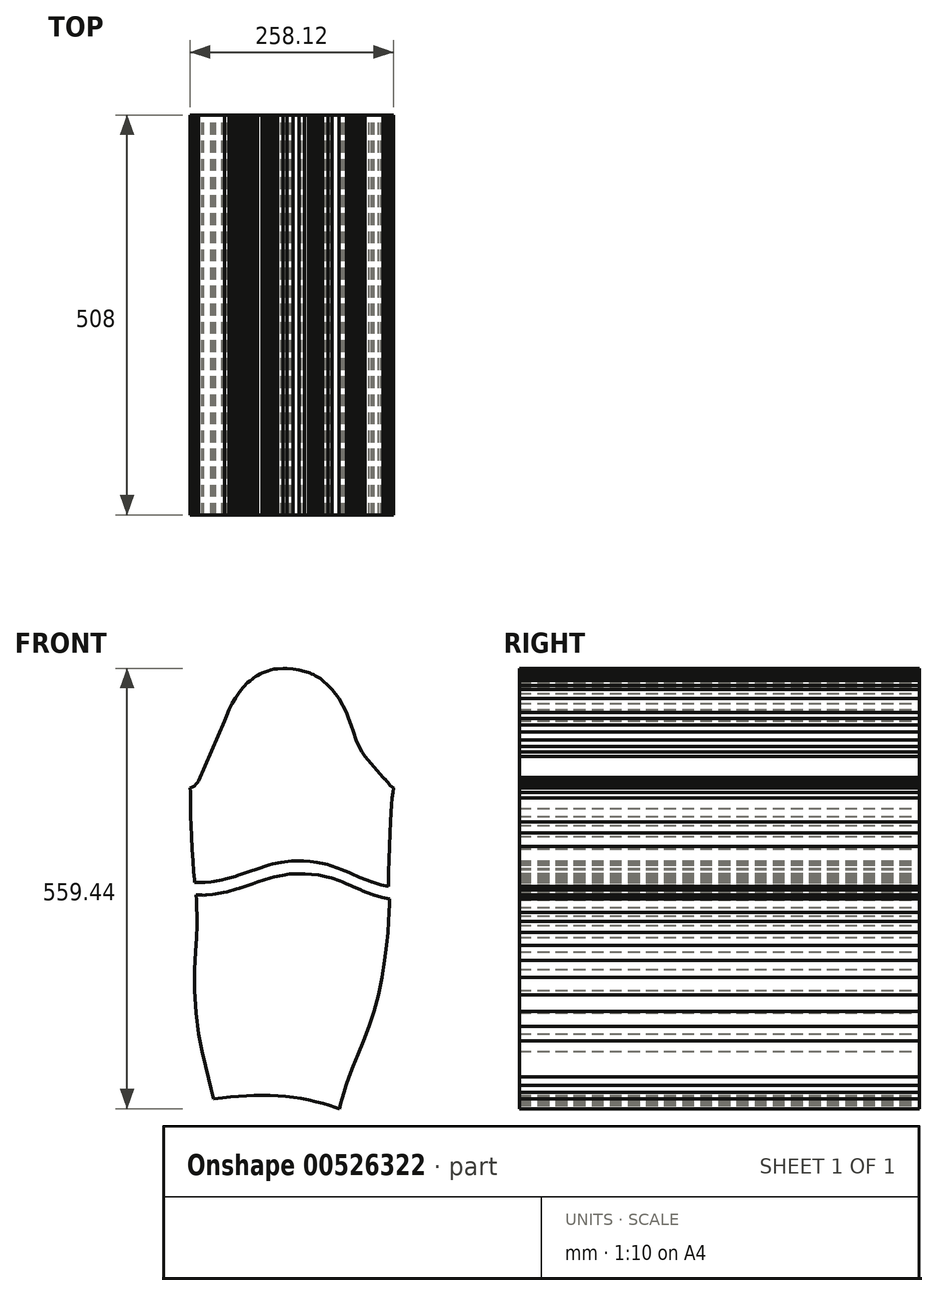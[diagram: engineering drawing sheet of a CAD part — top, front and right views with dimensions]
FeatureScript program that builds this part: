
annotation { "Feature Type Name" : "Feature", "Feature Type Description" : "" }
export const myFeature = defineFeature(function(context is Context, id is Id, definition is map)
    precondition{}
    {
        {
            var Q0;
            Q0=qCreatedBy(makeId("Front.planeOp"),FACE);
            var sketch = newSketch(context, id + "F0", { "sketchPlane" : qUnion([Q0])});
            skLineSegment(sketch, "E0", {"start": v(-129.06, 127.99) * mm, "end": v(-125.78, 128.92) * mm});
            skLineSegment(sketch, "E1", {"start": v(-125.78, 128.92) * mm, "end": v(-123.74, 130.52) * mm});
            skLineSegment(sketch, "E2", {"start": v(-123.74, 130.52) * mm, "end": v(-121.67, 132.71) * mm});
            skLineSegment(sketch, "E3", {"start": v(-121.67, 132.71) * mm, "end": v(-119.92, 134.96) * mm});
            skLineSegment(sketch, "E4", {"start": v(-119.92, 134.96) * mm, "end": v(-118.45, 136.86) * mm});
            skLineSegment(sketch, "E5", {"start": v(-118.45, 136.86) * mm, "end": v(-85.06, 212.65) * mm});
            skLineSegment(sketch, "E6", {"start": v(-85.06, 212.65) * mm, "end": v(-82.6, 219.33) * mm});
            skLineSegment(sketch, "E7", {"start": v(-82.6, 219.33) * mm, "end": v(-79.7, 227.1) * mm});
            skLineSegment(sketch, "E8", {"start": v(-79.7, 227.1) * mm, "end": v(-75.87, 235.03) * mm});
            skLineSegment(sketch, "E9", {"start": v(-75.87, 235.03) * mm, "end": v(-71.47, 242.22) * mm});
            skLineSegment(sketch, "E10", {"start": v(-71.47, 242.22) * mm, "end": v(-67.32, 247.98) * mm});
            skLineSegment(sketch, "E11", {"start": v(-67.32, 247.98) * mm, "end": v(-64.18, 252.12) * mm});
            skLineSegment(sketch, "E12", {"start": v(-64.18, 252.12) * mm, "end": v(-61.7, 255.53) * mm});
            skLineSegment(sketch, "E13", {"start": v(-61.7, 255.53) * mm, "end": v(-59.4, 257.84) * mm});
            skLineSegment(sketch, "E14", {"start": v(-59.4, 257.84) * mm, "end": v(-58.19, 259.5) * mm});
            skLineSegment(sketch, "E15", {"start": v(-58.19, 259.5) * mm, "end": v(-56.4, 261.46) * mm});
            skLineSegment(sketch, "E16", {"start": v(-56.4, 261.46) * mm, "end": v(-53.2, 263.83) * mm});
            skLineSegment(sketch, "E17", {"start": v(-53.2, 263.83) * mm, "end": v(-50.06, 266.24) * mm});
            skLineSegment(sketch, "E18", {"start": v(-50.06, 266.24) * mm, "end": v(-48.03, 267.92) * mm});
            skLineSegment(sketch, "E19", {"start": v(-48.03, 267.92) * mm, "end": v(-45.8, 269.31) * mm});
            skLineSegment(sketch, "E20", {"start": v(-45.8, 269.31) * mm, "end": v(-43.72, 270.77) * mm});
            skLineSegment(sketch, "E21", {"start": v(-43.72, 270.77) * mm, "end": v(-40.37, 272.52) * mm});
            skLineSegment(sketch, "E22", {"start": v(-40.37, 272.52) * mm, "end": v(-37.71, 273.92) * mm});
            skLineSegment(sketch, "E23", {"start": v(-37.71, 273.92) * mm, "end": v(-33.9, 275.3) * mm});
            skLineSegment(sketch, "E24", {"start": v(-33.9, 275.3) * mm, "end": v(-30.01, 276.47) * mm});
            skLineSegment(sketch, "E25", {"start": v(-30.01, 276.47) * mm, "end": v(-27.04, 277.54) * mm});
            skLineSegment(sketch, "E26", {"start": v(-27.04, 277.54) * mm, "end": v(-22.6, 278.6) * mm});
            skLineSegment(sketch, "E27", {"start": v(-22.6, 278.6) * mm, "end": v(-17.94, 279.04) * mm});
            skLineSegment(sketch, "E28", {"start": v(-17.94, 279.04) * mm, "end": v(-11.4, 279.5) * mm});
            skLineSegment(sketch, "E29", {"start": v(-11.4, 279.5) * mm, "end": v(-5.8, 279.72) * mm});
            skLineSegment(sketch, "E30", {"start": v(-5.8, 279.72) * mm, "end": v(1.6, 279.03) * mm});
            skLineSegment(sketch, "E31", {"start": v(1.6, 279.03) * mm, "end": v(9.41, 277.6) * mm});
            skLineSegment(sketch, "E32", {"start": v(9.41, 277.6) * mm, "end": v(16.28, 275.7) * mm});
            skLineSegment(sketch, "E33", {"start": v(16.28, 275.7) * mm, "end": v(21.23, 274.15) * mm});
            skLineSegment(sketch, "E34", {"start": v(21.23, 274.15) * mm, "end": v(23.5, 273.55) * mm});
            skLineSegment(sketch, "E35", {"start": v(23.5, 273.55) * mm, "end": v(25.19, 272.62) * mm});
            skLineSegment(sketch, "E36", {"start": v(25.19, 272.62) * mm, "end": v(27.5, 271.6) * mm});
            skLineSegment(sketch, "E37", {"start": v(27.5, 271.6) * mm, "end": v(30.25, 269.98) * mm});
            skLineSegment(sketch, "E38", {"start": v(30.25, 269.98) * mm, "end": v(32.91, 268.54) * mm});
            skLineSegment(sketch, "E39", {"start": v(32.91, 268.54) * mm, "end": v(36.27, 266.46) * mm});
            skLineSegment(sketch, "E40", {"start": v(36.27, 266.46) * mm, "end": v(39.3, 263.93) * mm});
            skLineSegment(sketch, "E41", {"start": v(39.3, 263.93) * mm, "end": v(46.3, 257.73) * mm});
            skLineSegment(sketch, "E42", {"start": v(46.3, 257.73) * mm, "end": v(51.38, 252.95) * mm});
            skLineSegment(sketch, "E43", {"start": v(51.38, 252.95) * mm, "end": v(55.72, 247.02) * mm});
            skLineSegment(sketch, "E44", {"start": v(55.72, 247.02) * mm, "end": v(59.84, 241.45) * mm});
            skLineSegment(sketch, "E45", {"start": v(59.84, 241.45) * mm, "end": v(69.25, 223.53) * mm});
            skLineSegment(sketch, "E46", {"start": v(69.25, 223.53) * mm, "end": v(71.89, 216.2) * mm});
            skLineSegment(sketch, "E47", {"start": v(71.89, 216.2) * mm, "end": v(75.36, 208) * mm});
            skLineSegment(sketch, "E48", {"start": v(75.36, 208) * mm, "end": v(78.39, 198.63) * mm});
            skLineSegment(sketch, "E49", {"start": v(78.39, 198.63) * mm, "end": v(81.28, 188.97) * mm});
            skLineSegment(sketch, "E50", {"start": v(81.28, 188.97) * mm, "end": v(85.37, 180.55) * mm});
            skLineSegment(sketch, "E51", {"start": v(85.37, 180.55) * mm, "end": v(89.27, 173.34) * mm});
            skLineSegment(sketch, "E52", {"start": v(89.27, 173.34) * mm, "end": v(93, 167.63) * mm});
            skLineSegment(sketch, "E53", {"start": v(93, 167.63) * mm, "end": v(116.08, 141.22) * mm});
            skLineSegment(sketch, "E54", {"start": v(116.08, 141.22) * mm, "end": v(117.67, 139.44) * mm});
            skLineSegment(sketch, "E55", {"start": v(117.67, 139.44) * mm, "end": v(118.96, 138.2) * mm});
            skLineSegment(sketch, "E56", {"start": v(118.96, 138.2) * mm, "end": v(120.13, 136.65) * mm});
            skLineSegment(sketch, "E57", {"start": v(120.13, 136.65) * mm, "end": v(121.99, 134.64) * mm});
            skLineSegment(sketch, "E58", {"start": v(121.99, 134.64) * mm, "end": v(124.73, 131.11) * mm});
            skLineSegment(sketch, "E59", {"start": v(124.73, 131.11) * mm, "end": v(129.06, 127.9) * mm});
            skLineSegment(sketch, "E60", {"start": v(129.06, 127.9) * mm, "end": v(128.28, 121.94) * mm});
            skLineSegment(sketch, "E61", {"start": v(128.28, 121.94) * mm, "end": v(127.6, 114.85) * mm});
            skLineSegment(sketch, "E62", {"start": v(127.6, 114.85) * mm, "end": v(126.92, 106.4) * mm});
            skLineSegment(sketch, "E63", {"start": v(126.92, 106.4) * mm, "end": v(126.18, 96.34) * mm});
            skLineSegment(sketch, "E64", {"start": v(126.18, 96.34) * mm, "end": v(125.4, 84.41) * mm});
            skLineSegment(sketch, "E65", {"start": v(125.4, 84.41) * mm, "end": v(124.62, 70.26) * mm});
            skLineSegment(sketch, "E66", {"start": v(124.62, 70.26) * mm, "end": v(123.94, 53.44) * mm});
            skLineSegment(sketch, "E67", {"start": v(123.94, 53.44) * mm, "end": v(123.45, 36.05) * mm});
            skLineSegment(sketch, "E68", {"start": v(123.45, 36.05) * mm, "end": v(123.1, 20.74) * mm});
            skLineSegment(sketch, "E69", {"start": v(123.1, 20.74) * mm, "end": v(122.77, 7.64) * mm});
            skLineSegment(sketch, "E70", {"start": v(122.77, 7.64) * mm, "end": v(122.6, 2.87) * mm});
            skLineSegment(sketch, "E71", {"start": v(122.6, 2.87) * mm, "end": v(116.26, 4.18) * mm});
            skLineSegment(sketch, "E72", {"start": v(116.26, 4.18) * mm, "end": v(113.1, 4.8) * mm});
            skLineSegment(sketch, "E73", {"start": v(113.1, 4.8) * mm, "end": v(102, 8.01) * mm});
            skLineSegment(sketch, "E74", {"start": v(102, 8.01) * mm, "end": v(101.15, 8.25) * mm});
            skLineSegment(sketch, "E75", {"start": v(101.15, 8.25) * mm, "end": v(100.98, 8.32) * mm});
            skLineSegment(sketch, "E76", {"start": v(100.98, 8.32) * mm, "end": v(100.06, 8.68) * mm});
            skLineSegment(sketch, "E77", {"start": v(100.06, 8.68) * mm, "end": v(88.25, 13.28) * mm});
            skLineSegment(sketch, "E78", {"start": v(88.25, 13.28) * mm, "end": v(86.15, 14.09) * mm});
            skLineSegment(sketch, "E79", {"start": v(86.15, 14.09) * mm, "end": v(75.3, 18.88) * mm});
            skLineSegment(sketch, "E80", {"start": v(75.3, 18.88) * mm, "end": v(72.52, 20.08) * mm});
            skLineSegment(sketch, "E81", {"start": v(72.52, 20.08) * mm, "end": v(67.7, 22.18) * mm});
            skLineSegment(sketch, "E82", {"start": v(67.7, 22.18) * mm, "end": v(62.7, 24.37) * mm});
            skLineSegment(sketch, "E83", {"start": v(62.7, 24.37) * mm, "end": v(59.36, 25.76) * mm});
            skLineSegment(sketch, "E84", {"start": v(59.36, 25.76) * mm, "end": v(48.53, 29.38) * mm});
            skLineSegment(sketch, "E85", {"start": v(48.53, 29.38) * mm, "end": v(45.64, 30.34) * mm});
            skLineSegment(sketch, "E86", {"start": v(45.64, 30.34) * mm, "end": v(42.36, 31.17) * mm});
            skLineSegment(sketch, "E87", {"start": v(42.36, 31.17) * mm, "end": v(32.12, 33.1) * mm});
            skLineSegment(sketch, "E88", {"start": v(32.12, 33.1) * mm, "end": v(23.04, 34.23) * mm});
            skLineSegment(sketch, "E89", {"start": v(23.04, 34.23) * mm, "end": v(15.13, 34.8) * mm});
            skLineSegment(sketch, "E90", {"start": v(15.13, 34.8) * mm, "end": v(-0.5, 34.69) * mm});
            skLineSegment(sketch, "E91", {"start": v(-0.5, 34.69) * mm, "end": v(-4.82, 34.6) * mm});
            skLineSegment(sketch, "E92", {"start": v(-4.82, 34.6) * mm, "end": v(-13.8, 32.87) * mm});
            skLineSegment(sketch, "E93", {"start": v(-13.8, 32.87) * mm, "end": v(-24.33, 30.99) * mm});
            skLineSegment(sketch, "E94", {"start": v(-24.33, 30.99) * mm, "end": v(-28.64, 29.75) * mm});
            skLineSegment(sketch, "E95", {"start": v(-28.64, 29.75) * mm, "end": v(-45.2, 24.49) * mm});
            skLineSegment(sketch, "E96", {"start": v(-45.2, 24.49) * mm, "end": v(-51.53, 22.25) * mm});
            skLineSegment(sketch, "E97", {"start": v(-51.53, 22.25) * mm, "end": v(-66.86, 16.9) * mm});
            skLineSegment(sketch, "E98", {"start": v(-66.86, 16.9) * mm, "end": v(-67.43, 16.71) * mm});
            skLineSegment(sketch, "E99", {"start": v(-67.43, 16.71) * mm, "end": v(-68.62, 16.33) * mm});
            skLineSegment(sketch, "E100", {"start": v(-68.62, 16.33) * mm, "end": v(-71.7, 15.5) * mm});
            skLineSegment(sketch, "E101", {"start": v(-71.7, 15.5) * mm, "end": v(-84, 12.04) * mm});
            skLineSegment(sketch, "E102", {"start": v(-84, 12.04) * mm, "end": v(-88.47, 11.04) * mm});
            skLineSegment(sketch, "E103", {"start": v(-88.47, 11.04) * mm, "end": v(-98.66, 9.15) * mm});
            skLineSegment(sketch, "E104", {"start": v(-98.66, 9.15) * mm, "end": v(-102.44, 8.55) * mm});
            skLineSegment(sketch, "E105", {"start": v(-102.44, 8.55) * mm, "end": v(-110.4, 7.93) * mm});
            skLineSegment(sketch, "E106", {"start": v(-110.4, 7.93) * mm, "end": v(-113.6, 7.68) * mm});
            skLineSegment(sketch, "E107", {"start": v(-113.6, 7.68) * mm, "end": v(-116.64, 7.7) * mm});
            skLineSegment(sketch, "E108", {"start": v(-116.64, 7.7) * mm, "end": v(-123.46, 7.78) * mm});
            skLineSegment(sketch, "E109", {"start": v(-123.46, 7.78) * mm, "end": v(-123.66, 10.72) * mm});
            skLineSegment(sketch, "E110", {"start": v(-123.66, 10.72) * mm, "end": v(-124.49, 21.76) * mm});
            skLineSegment(sketch, "E111", {"start": v(-124.49, 21.76) * mm, "end": v(-125.5, 34.65) * mm});
            skLineSegment(sketch, "E112", {"start": v(-125.5, 34.65) * mm, "end": v(-126.62, 50.2) * mm});
            skLineSegment(sketch, "E113", {"start": v(-126.62, 50.2) * mm, "end": v(-127.52, 66.05) * mm});
            skLineSegment(sketch, "E114", {"start": v(-127.52, 66.05) * mm, "end": v(-128.1, 79.86) * mm});
            skLineSegment(sketch, "E115", {"start": v(-128.1, 79.86) * mm, "end": v(-128.43, 91.56) * mm});
            skLineSegment(sketch, "E116", {"start": v(-128.43, 91.56) * mm, "end": v(-128.6, 101.4) * mm});
            skLineSegment(sketch, "E117", {"start": v(-128.6, 101.4) * mm, "end": v(-128.65, 109.84) * mm});
            skLineSegment(sketch, "E118", {"start": v(-128.65, 109.84) * mm, "end": v(-128.7, 116.9) * mm});
            skLineSegment(sketch, "E119", {"start": v(-128.7, 116.9) * mm, "end": v(-128.76, 122.9) * mm});
            skLineSegment(sketch, "E120", {"start": v(-128.76, 122.9) * mm, "end": v(-129.06, 127.99) * mm});
            skLineSegment(sketch, "E121", {"start": v(-87.7, -265.91) * mm, "end": v(-99.36, -267.16) * mm});
            skLineSegment(sketch, "E122", {"start": v(-99.36, -267.16) * mm, "end": v(-102.24, -254.86) * mm});
            skLineSegment(sketch, "E123", {"start": v(-102.24, -254.86) * mm, "end": v(-105.54, -241.28) * mm});
            skLineSegment(sketch, "E124", {"start": v(-105.54, -241.28) * mm, "end": v(-109.4, -225.58) * mm});
            skLineSegment(sketch, "E125", {"start": v(-109.4, -225.58) * mm, "end": v(-113.8, -207) * mm});
            skLineSegment(sketch, "E126", {"start": v(-113.8, -207) * mm, "end": v(-118.22, -184.67) * mm});
            skLineSegment(sketch, "E127", {"start": v(-118.22, -184.67) * mm, "end": v(-121.8, -157.96) * mm});
            skLineSegment(sketch, "E128", {"start": v(-121.8, -157.96) * mm, "end": v(-123.6, -129.31) * mm});
            skLineSegment(sketch, "E129", {"start": v(-123.6, -129.31) * mm, "end": v(-123.45, -102.96) * mm});
            skLineSegment(sketch, "E130", {"start": v(-123.45, -102.96) * mm, "end": v(-122.29, -80.62) * mm});
            skLineSegment(sketch, "E131", {"start": v(-122.29, -80.62) * mm, "end": v(-121.14, -62.26) * mm});
            skLineSegment(sketch, "E132", {"start": v(-121.14, -62.26) * mm, "end": v(-120.48, -47.14) * mm});
            skLineSegment(sketch, "E133", {"start": v(-120.48, -47.14) * mm, "end": v(-120.42, -34.55) * mm});
            skLineSegment(sketch, "E134", {"start": v(-120.42, -34.55) * mm, "end": v(-120.76, -23.9) * mm});
            skLineSegment(sketch, "E135", {"start": v(-120.76, -23.9) * mm, "end": v(-121.24, -14.8) * mm});
            skLineSegment(sketch, "E136", {"start": v(-121.24, -14.8) * mm, "end": v(-121.67, -8.4) * mm});
            skLineSegment(sketch, "E137", {"start": v(-121.67, -8.4) * mm, "end": v(-114.85, -8.49) * mm});
            skLineSegment(sketch, "E138", {"start": v(-114.85, -8.49) * mm, "end": v(-111.81, -8.5) * mm});
            skLineSegment(sketch, "E139", {"start": v(-111.81, -8.5) * mm, "end": v(-108.62, -8.26) * mm});
            skLineSegment(sketch, "E140", {"start": v(-108.62, -8.26) * mm, "end": v(-100.65, -7.64) * mm});
            skLineSegment(sketch, "E141", {"start": v(-100.65, -7.64) * mm, "end": v(-96.86, -7.03) * mm});
            skLineSegment(sketch, "E142", {"start": v(-96.86, -7.03) * mm, "end": v(-86.68, -5.15) * mm});
            skLineSegment(sketch, "E143", {"start": v(-86.68, -5.15) * mm, "end": v(-82.2, -4.15) * mm});
            skLineSegment(sketch, "E144", {"start": v(-82.2, -4.15) * mm, "end": v(-69.9, -0.7) * mm});
            skLineSegment(sketch, "E145", {"start": v(-69.9, -0.7) * mm, "end": v(-66.82, 0.15) * mm});
            skLineSegment(sketch, "E146", {"start": v(-66.82, 0.15) * mm, "end": v(-65.63, 0.53) * mm});
            skLineSegment(sketch, "E147", {"start": v(-65.63, 0.53) * mm, "end": v(-65.07, 0.72) * mm});
            skLineSegment(sketch, "E148", {"start": v(-65.07, 0.72) * mm, "end": v(-49.74, 6.07) * mm});
            skLineSegment(sketch, "E149", {"start": v(-49.74, 6.07) * mm, "end": v(-43.4, 8.3) * mm});
            skLineSegment(sketch, "E150", {"start": v(-43.4, 8.3) * mm, "end": v(-26.85, 13.57) * mm});
            skLineSegment(sketch, "E151", {"start": v(-26.85, 13.57) * mm, "end": v(-22.54, 14.8) * mm});
            skLineSegment(sketch, "E152", {"start": v(-22.54, 14.8) * mm, "end": v(-12, 16.69) * mm});
            skLineSegment(sketch, "E153", {"start": v(-12, 16.69) * mm, "end": v(-3.03, 18.4) * mm});
            skLineSegment(sketch, "E154", {"start": v(-3.03, 18.4) * mm, "end": v(1.3, 18.5) * mm});
            skLineSegment(sketch, "E155", {"start": v(1.3, 18.5) * mm, "end": v(16.93, 18.62) * mm});
            skLineSegment(sketch, "E156", {"start": v(16.93, 18.62) * mm, "end": v(24.83, 18.05) * mm});
            skLineSegment(sketch, "E157", {"start": v(24.83, 18.05) * mm, "end": v(33.92, 16.92) * mm});
            skLineSegment(sketch, "E158", {"start": v(33.92, 16.92) * mm, "end": v(44.15, 14.98) * mm});
            skLineSegment(sketch, "E159", {"start": v(44.15, 14.98) * mm, "end": v(47.44, 14.16) * mm});
            skLineSegment(sketch, "E160", {"start": v(47.44, 14.16) * mm, "end": v(50.33, 13.2) * mm});
            skLineSegment(sketch, "E161", {"start": v(50.33, 13.2) * mm, "end": v(61.15, 9.58) * mm});
            skLineSegment(sketch, "E162", {"start": v(61.15, 9.58) * mm, "end": v(64.49, 8.19) * mm});
            skLineSegment(sketch, "E163", {"start": v(64.49, 8.19) * mm, "end": v(69.5, 6) * mm});
            skLineSegment(sketch, "E164", {"start": v(69.5, 6) * mm, "end": v(74.32, 3.9) * mm});
            skLineSegment(sketch, "E165", {"start": v(74.32, 3.9) * mm, "end": v(77.09, 2.7) * mm});
            skLineSegment(sketch, "E166", {"start": v(77.09, 2.7) * mm, "end": v(87.94, -2.1) * mm});
            skLineSegment(sketch, "E167", {"start": v(87.94, -2.1) * mm, "end": v(90.05, -2.9) * mm});
            skLineSegment(sketch, "E168", {"start": v(90.05, -2.9) * mm, "end": v(101.85, -7.5) * mm});
            skLineSegment(sketch, "E169", {"start": v(101.85, -7.5) * mm, "end": v(102.77, -7.87) * mm});
            skLineSegment(sketch, "E170", {"start": v(102.77, -7.87) * mm, "end": v(102.94, -7.93) * mm});
            skLineSegment(sketch, "E171", {"start": v(102.94, -7.93) * mm, "end": v(103.8, -8.18) * mm});
            skLineSegment(sketch, "E172", {"start": v(103.8, -8.18) * mm, "end": v(114.9, -11.38) * mm});
            skLineSegment(sketch, "E173", {"start": v(114.9, -11.38) * mm, "end": v(118.05, -12) * mm});
            skLineSegment(sketch, "E174", {"start": v(118.05, -12) * mm, "end": v(124.4, -13.32) * mm});
            skLineSegment(sketch, "E175", {"start": v(124.4, -13.32) * mm, "end": v(124.2, -19.73) * mm});
            skLineSegment(sketch, "E176", {"start": v(124.2, -19.73) * mm, "end": v(123.76, -30.22) * mm});
            skLineSegment(sketch, "E177", {"start": v(123.76, -30.22) * mm, "end": v(123.13, -41.87) * mm});
            skLineSegment(sketch, "E178", {"start": v(123.13, -41.87) * mm, "end": v(122.13, -55.73) * mm});
            skLineSegment(sketch, "E179", {"start": v(122.13, -55.73) * mm, "end": v(120.58, -72.16) * mm});
            skLineSegment(sketch, "E180", {"start": v(120.58, -72.16) * mm, "end": v(118.1, -91.62) * mm});
            skLineSegment(sketch, "E181", {"start": v(118.1, -91.62) * mm, "end": v(114.57, -113.12) * mm});
            skLineSegment(sketch, "E182", {"start": v(114.57, -113.12) * mm, "end": v(109.97, -134.97) * mm});
            skLineSegment(sketch, "E183", {"start": v(109.97, -134.97) * mm, "end": v(104.24, -155.86) * mm});
            skLineSegment(sketch, "E184", {"start": v(104.24, -155.86) * mm, "end": v(97.88, -175.22) * mm});
            skLineSegment(sketch, "E185", {"start": v(97.88, -175.22) * mm, "end": v(90.96, -193.3) * mm});
            skLineSegment(sketch, "E186", {"start": v(90.96, -193.3) * mm, "end": v(84.09, -210.56) * mm});
            skLineSegment(sketch, "E187", {"start": v(84.09, -210.56) * mm, "end": v(78, -226.2) * mm});
            skLineSegment(sketch, "E188", {"start": v(78, -226.2) * mm, "end": v(72.87, -239.23) * mm});
            skLineSegment(sketch, "E189", {"start": v(72.87, -239.23) * mm, "end": v(68.92, -250.06) * mm});
            skLineSegment(sketch, "E190", {"start": v(68.92, -250.06) * mm, "end": v(66.07, -259.26) * mm});
            skLineSegment(sketch, "E191", {"start": v(66.07, -259.26) * mm, "end": v(63.86, -267.16) * mm});
            skLineSegment(sketch, "E192", {"start": v(63.86, -267.16) * mm, "end": v(62.1, -273.9) * mm});
            skLineSegment(sketch, "E193", {"start": v(62.1, -273.9) * mm, "end": v(60.62, -279.72) * mm});
            skLineSegment(sketch, "E194", {"start": v(60.62, -279.72) * mm, "end": v(54.7, -277.8) * mm});
            skLineSegment(sketch, "E195", {"start": v(54.7, -277.8) * mm, "end": v(47.86, -275.62) * mm});
            skLineSegment(sketch, "E196", {"start": v(47.86, -275.62) * mm, "end": v(39.78, -273.22) * mm});
            skLineSegment(sketch, "E197", {"start": v(39.78, -273.22) * mm, "end": v(30.7, -270.84) * mm});
            skLineSegment(sketch, "E198", {"start": v(30.7, -270.84) * mm, "end": v(21.4, -268.69) * mm});
            skLineSegment(sketch, "E199", {"start": v(21.4, -268.69) * mm, "end": v(11.78, -266.76) * mm});
            skLineSegment(sketch, "E200", {"start": v(11.78, -266.76) * mm, "end": v(1.94, -265.26) * mm});
            skLineSegment(sketch, "E201", {"start": v(1.94, -265.26) * mm, "end": v(-7.7, -264.14) * mm});
            skLineSegment(sketch, "E202", {"start": v(-7.7, -264.14) * mm, "end": v(-17.62, -263.34) * mm});
            skLineSegment(sketch, "E203", {"start": v(-17.62, -263.34) * mm, "end": v(-27.55, -262.83) * mm});
            skLineSegment(sketch, "E204", {"start": v(-27.55, -262.83) * mm, "end": v(-37.62, -262.62) * mm});
            skLineSegment(sketch, "E205", {"start": v(-37.62, -262.62) * mm, "end": v(-47.84, -262.75) * mm});
            skLineSegment(sketch, "E206", {"start": v(-47.84, -262.75) * mm, "end": v(-57.63, -263.2) * mm});
            skLineSegment(sketch, "E207", {"start": v(-57.63, -263.2) * mm, "end": v(-67.69, -263.95) * mm});
            skLineSegment(sketch, "E208", {"start": v(-67.69, -263.95) * mm, "end": v(-77.64, -264.89) * mm});
            skLineSegment(sketch, "E209", {"start": v(-77.64, -264.89) * mm, "end": v(-87.7, -265.91) * mm});
            skLineSegment(sketch, "E210.bottom", {"start": v(-335.92, 106.88) * mm, "end": v(-172.45, 106.88) * mm});
            skLineSegment(sketch, "E210.top", {"start": v(-335.92, -76.34) * mm, "end": v(-172.45, -76.34) * mm});
            skLineSegment(sketch, "E210.left", {"start": v(-335.92, 106.88) * mm, "end": v(-335.92, -76.34) * mm});
            skLineSegment(sketch, "E210.right", {"start": v(-172.45, 106.88) * mm, "end": v(-172.45, -76.34) * mm});
            skLineSegment(sketch, "E211.bottom", {"start": v(-172.45, 22.45) * mm, "end": v(-335.92, 22.45) * mm});
            skLineSegment(sketch, "E211.top", {"start": v(-172.45, 15.27) * mm, "end": v(-335.92, 15.27) * mm});
            skLineSegment(sketch, "E211.left", {"start": v(-172.45, 22.45) * mm, "end": v(-172.45, 15.27) * mm});
            skLineSegment(sketch, "E211.right", {"start": v(-335.92, 22.45) * mm, "end": v(-335.92, 15.27) * mm});
            skSolve(sketch);
        }
        {
            var Q0;
            Q0=sQuery(id+"F0.wireOp",EDGE,"E210.bottom");
            var Q1;
            Q1=sQuery(id+"F0.wireOp",EDGE,"E210.right");
            var Q2;
            Q2=sQuery(id+"F0.wireOp",EDGE,"E210.left");
            var Q3;
            Q3=sQuery(id+"F0.wireOp",EDGE,"E210.top");
            extrude(context, id + "F1", {"bodyType" : ToolBodyType.SURFACE, "surfaceEntities" : qUnion([Q0, Q1, Q2, Q3]), "depth" : 254 * mm, "offsetDistance" : 25.4 * mm});
        }
        {
            var Q0;
            Q0=makeQuery(id+"F0.imprint","IMPRINT",FACE,{"disambiguationData":[TD([[makeQuery(id+"F0.imprint","IMPRINT",EDGE,{"derivedFrom":sQuery(id+"F0.wireOp",EDGE,"E121")}),-1.0]])]});
            var Q1;
            Q1=makeQuery(id+"F0.imprint","IMPRINT",FACE,{"disambiguationData":[TD([[makeQuery(id+"F0.imprint","IMPRINT",EDGE,{"derivedFrom":sQuery(id+"F0.wireOp",EDGE,"E0")}),-1.0]])]});
            extrude(context, id + "F2", {"entities" : qUnion([Q0, Q1]), "depth" : 508 * mm, "offsetDistance" : 25.4 * mm});
        }
    });
